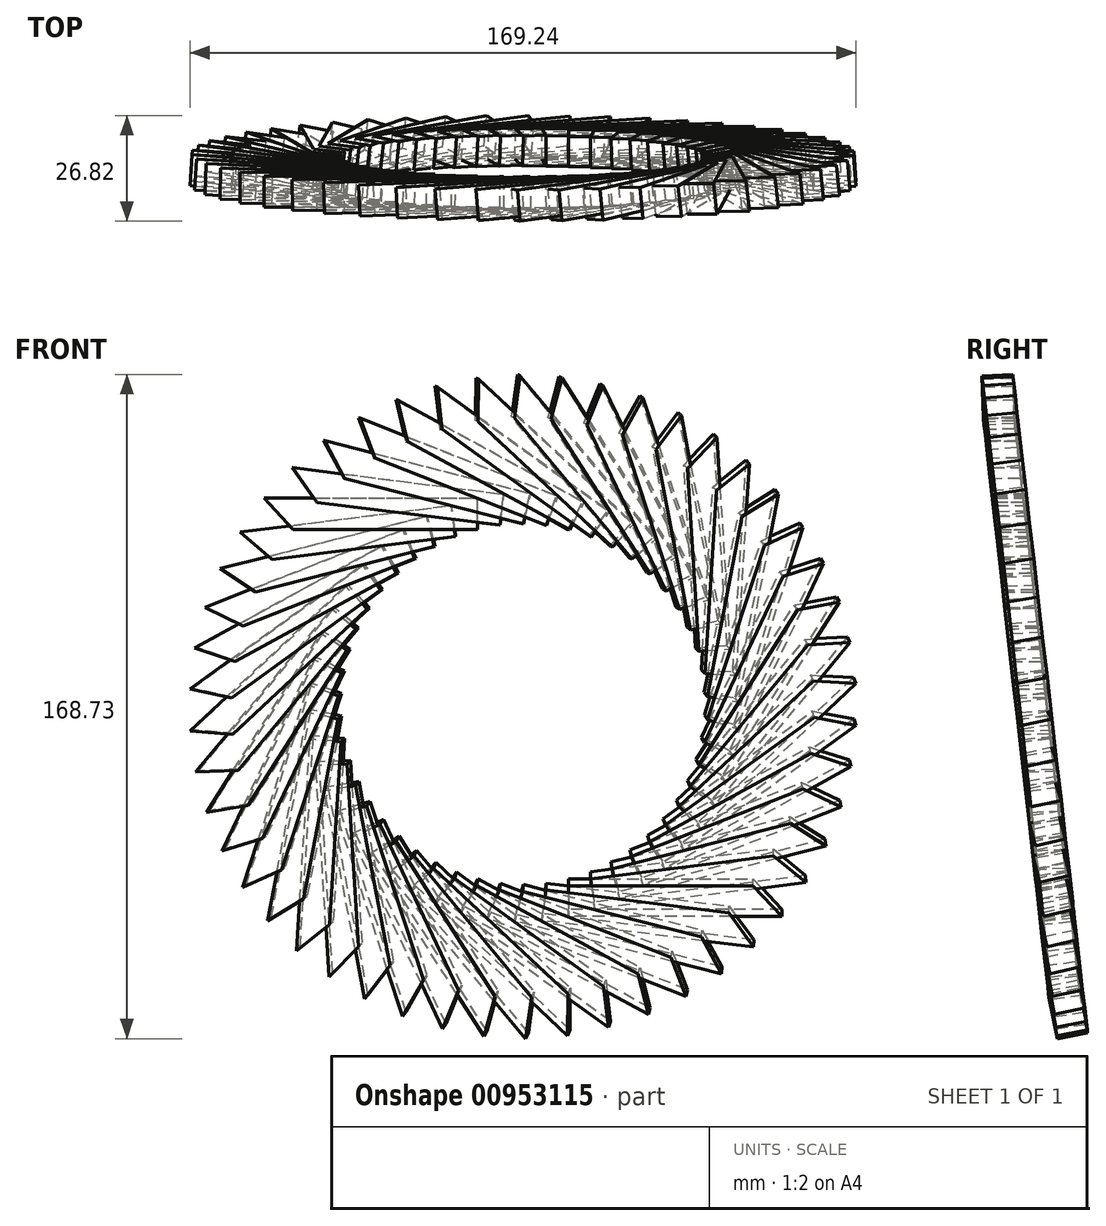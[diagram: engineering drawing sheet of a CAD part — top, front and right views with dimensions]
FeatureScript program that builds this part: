
annotation { "Feature Type Name" : "Feature", "Feature Type Description" : "" }
export const myFeature = defineFeature(function(context is Context, id is Id, definition is map)
    precondition{}
    {
        {
            var Q0;
            Q0=qCreatedBy(makeId("Front.planeOp"),FACE);
            var sketch = newSketch(context, id + "F0", { "sketchPlane" : qUnion([Q0])});
            skLineSegment(sketch, "E0", {"start": v(-24.83, 44.95) * mm, "end": v(-11.6, 44.95) * mm});
            skLineSegment(sketch, "E1", {"start": v(-11.6, 44.95) * mm, "end": v(-11.6, 52.92) * mm});
            skLineSegment(sketch, "E2", {"start": v(-11.6, 52.92) * mm, "end": v(-26.91, 52.92) * mm});
            skLineSegment(sketch, "E3", {"start": v(-24.83, 44.95) * mm, "end": v(-58.45, 44.95) * mm});
            skLineSegment(sketch, "E4", {"start": v(-58.45, 44.95) * mm, "end": v(-65.75, 52.92) * mm});
            skLineSegment(sketch, "E5", {"start": v(-65.75, 52.92) * mm, "end": v(-26.91, 52.92) * mm});
            skLineSegment(sketch, "E6", {"start": v(-26.91, 52.92) * mm, "end": v(-24.83, 44.95) * mm});
            skSolve(sketch);
        }
        {
            var Q0;
            Q0=makeQuery(id+"F0.imprint","IMPRINT",FACE,{"disambiguationData":[TD([[makeQuery(id+"F0.imprint","IMPRINT",EDGE,{"derivedFrom":sQuery(id+"F0.wireOp",EDGE,"E3")}),-1.0]])]});
            var Q1;
            Q1=makeQuery(id+"F0.imprint","IMPRINT",FACE,{"disambiguationData":[TD([[makeQuery(id+"F0.imprint","IMPRINT",EDGE,{"derivedFrom":sQuery(id+"F0.wireOp",EDGE,"E0")}),1.0]])]});
            extrude(context, id + "F1", {"entities" : qUnion([Q0, Q1]), "depth" : 7.87 * mm, "offsetDistance" : 25.4 * mm});
        }
        {
            var Q0;
            Q0=qCreatedBy(makeId("Right.planeOp"),FACE);
            var sketch = newSketch(context, id + "F2", { "sketchPlane" : qUnion([Q0])});
            skLineSegment(sketch, "E7", {"start": v(0, 0) * mm, "end": v(38.03, 4.31) * mm});
            skSolve(sketch);
        }
        {
            var Q0;
            Q0=makeQuery(id+"F1.opExtrude","SWEPT_BODY",BODY,{"disambiguationData":[OSD([sQuery(id+"F0.wireOp",EDGE,"E0"),sQuery(id+"F0.wireOp",EDGE,"E1"),sQuery(id+"F0.wireOp",EDGE,"E2"),sQuery(id+"F0.wireOp",EDGE,"E3"),sQuery(id+"F0.wireOp",EDGE,"E4"),sQuery(id+"F0.wireOp",EDGE,"E5")])]});
            var Q1;
            Q1=sQuery(id+"F2.wireOp",EDGE,"E7");
            circularPattern(context, id + "F3", {"entities" : qUnion([Q0]), "axis" : qUnion([Q1]), "angle" : 360 * degree, "instanceCount" : 50, "equalSpace" : true});
        }
    });
